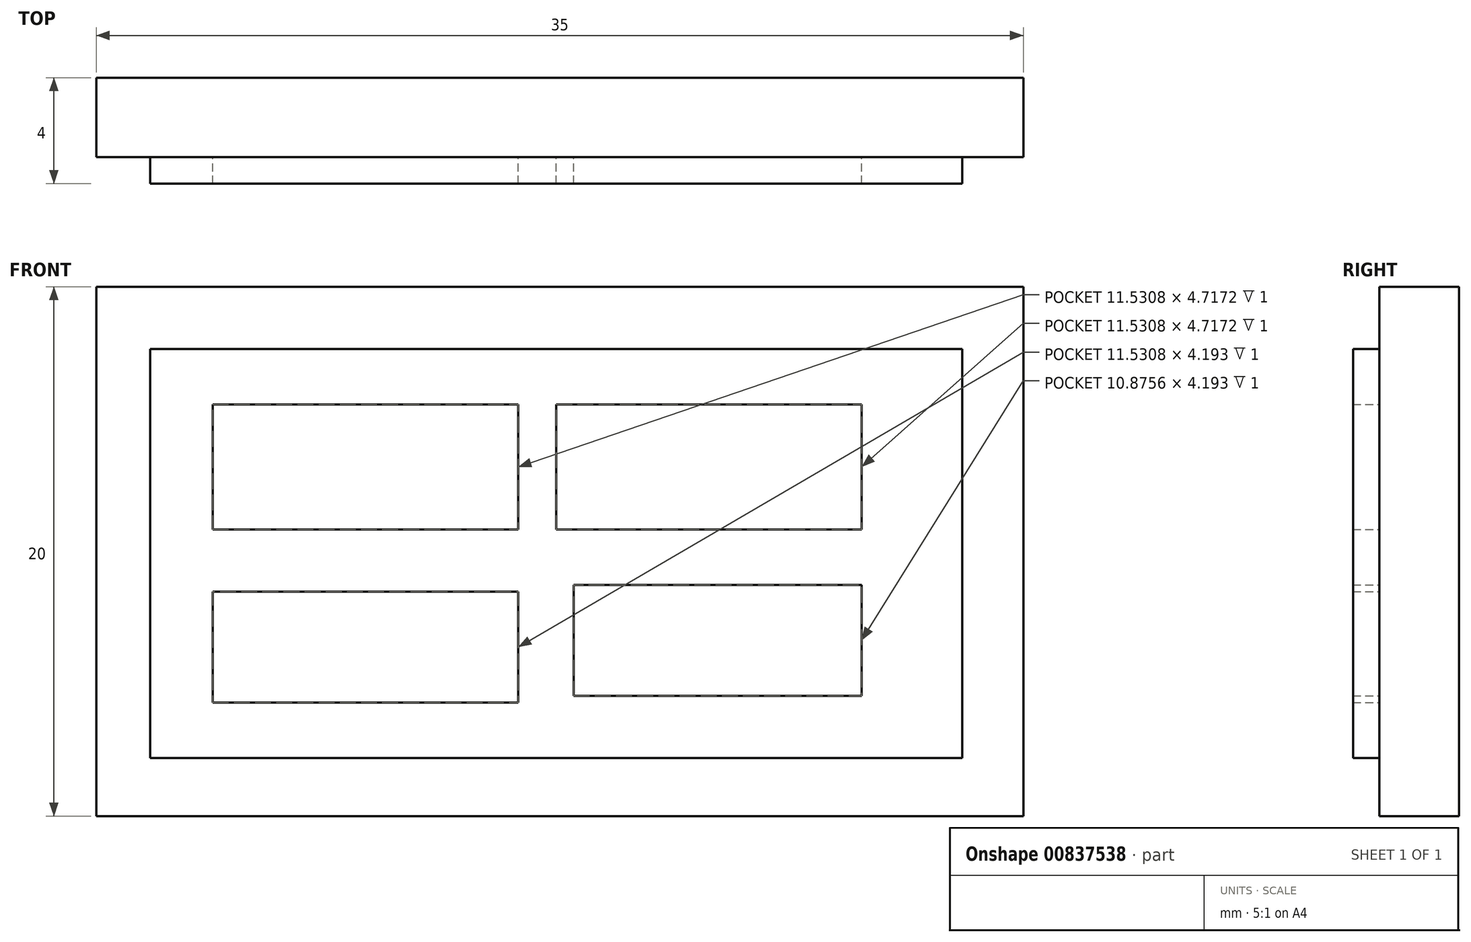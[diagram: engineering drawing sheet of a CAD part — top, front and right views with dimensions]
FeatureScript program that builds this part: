
annotation { "Feature Type Name" : "Feature", "Feature Type Description" : "" }
export const myFeature = defineFeature(function(context is Context, id is Id, definition is map)
    precondition{}
    {
        {
            var Q0;
            Q0=qCreatedBy(makeId("Front.planeOp"),FACE);
            var sketch = newSketch(context, id + "F0", { "sketchPlane" : qUnion([Q0])});
            skLineSegment(sketch, "E0.bottom", {"start": v(-28.9, -6.82) * mm, "end": v(6.1, -6.82) * mm});
            skLineSegment(sketch, "E0.top", {"start": v(-28.9, -26.82) * mm, "end": v(6.1, -26.82) * mm});
            skLineSegment(sketch, "E0.left", {"start": v(-28.9, -6.82) * mm, "end": v(-28.9, -26.82) * mm});
            skLineSegment(sketch, "E0.right", {"start": v(6.1, -6.82) * mm, "end": v(6.1, -26.82) * mm});
            skLineSegment(sketch, "E1.bottom", {"start": v(-26.86, -9.17) * mm, "end": v(3.8, -9.17) * mm});
            skLineSegment(sketch, "E1.top", {"start": v(-26.86, -24.63) * mm, "end": v(3.8, -24.63) * mm});
            skLineSegment(sketch, "E1.left", {"start": v(-26.86, -9.17) * mm, "end": v(-26.86, -24.63) * mm});
            skLineSegment(sketch, "E1.right", {"start": v(3.8, -9.17) * mm, "end": v(3.8, -24.63) * mm});
            skLineSegment(sketch, "E2.bottom", {"start": v(-24.5, -11.27) * mm, "end": v(-12.97, -11.27) * mm});
            skLineSegment(sketch, "E2.top", {"start": v(-24.5, -15.99) * mm, "end": v(-12.97, -15.99) * mm});
            skLineSegment(sketch, "E2.left", {"start": v(-24.5, -11.27) * mm, "end": v(-24.5, -15.99) * mm});
            skLineSegment(sketch, "E2.right", {"start": v(-12.97, -11.27) * mm, "end": v(-12.97, -15.99) * mm});
            skPoint(sketch, "E3.firstSnap0", {"position": v(-11.53, -9.17) * mm});
            skLineSegment(sketch, "E3.bottom", {"start": v(-11.53, -11.27) * mm, "end": v(0, -11.27) * mm});
            skLineSegment(sketch, "E3.top", {"start": v(-11.53, -15.99) * mm, "end": v(0, -15.99) * mm});
            skLineSegment(sketch, "E3.left", {"start": v(-11.53, -11.27) * mm, "end": v(-11.53, -15.99) * mm});
            skLineSegment(sketch, "E3.right", {"start": v(0, -11.27) * mm, "end": v(0, -15.99) * mm});
            skLineSegment(sketch, "E4.bottom", {"start": v(-24.5, -18.34) * mm, "end": v(-12.97, -18.34) * mm});
            skLineSegment(sketch, "E4.top", {"start": v(-24.5, -22.54) * mm, "end": v(-12.97, -22.54) * mm});
            skLineSegment(sketch, "E4.left", {"start": v(-24.5, -18.34) * mm, "end": v(-24.5, -22.54) * mm});
            skLineSegment(sketch, "E4.right", {"start": v(-12.97, -18.34) * mm, "end": v(-12.97, -22.54) * mm});
            skLineSegment(sketch, "E5.bottom", {"start": v(-10.88, -18.08) * mm, "end": v(0, -18.08) * mm});
            skLineSegment(sketch, "E5.top", {"start": v(-10.88, -22.28) * mm, "end": v(0, -22.28) * mm});
            skLineSegment(sketch, "E5.left", {"start": v(-10.88, -18.08) * mm, "end": v(-10.88, -22.28) * mm});
            skLineSegment(sketch, "E5.right", {"start": v(0, -18.08) * mm, "end": v(0, -22.28) * mm});
            skSolve(sketch);
        }
        {
            var Q0;
            Q0=makeQuery(id+"F0.imprint","IMPRINT",FACE,{"disambiguationData":[TD([[makeQuery(id+"F0.imprint","IMPRINT",EDGE,{"derivedFrom":sQuery(id+"F0.wireOp",EDGE,"E1.bottom")}),-1.0]])]});
            extrude(context, id + "F1", {"entities" : qUnion([Q0]), "depth" : 1 * mm, "offsetDistance" : 25 * mm});
        }
        {
            var Q0;
            Q0=makeQuery(id+"F0.imprint","IMPRINT",FACE,{"disambiguationData":[TD([[makeQuery(id+"F0.imprint","IMPRINT",EDGE,{"derivedFrom":sQuery(id+"F0.wireOp",EDGE,"E0.bottom")}),-1.0]])]});
            extrude(context, id + "F2", {"entities" : qUnion([Q0]), "operationType" : NewBodyOperationType.ADD, "depth" : 2 * mm, "offsetDistance" : 25 * mm});
        }
        {
            var Q0;
            Q0 = qSketchRegion(id + "F0", true);
            var Q1;
            Q1=makeQuery(id+"F0.imprint","IMPRINT",FACE,{"disambiguationData":[TD([[makeQuery(id+"F0.imprint","IMPRINT",EDGE,{"derivedFrom":sQuery(id+"F0.wireOp",EDGE,"E3.bottom")}),-1.0]])]});
            var Q2;
            Q2=makeQuery(id+"F0.imprint","IMPRINT",FACE,{"disambiguationData":[TD([[makeQuery(id+"F0.imprint","IMPRINT",EDGE,{"derivedFrom":sQuery(id+"F0.wireOp",EDGE,"E4.bottom")}),-1.0]])]});
            var Q3;
            Q3=makeQuery(id+"F0.imprint","IMPRINT",FACE,{"disambiguationData":[TD([[makeQuery(id+"F0.imprint","IMPRINT",EDGE,{"derivedFrom":sQuery(id+"F0.wireOp",EDGE,"E5.bottom")}),-1.0]])]});
            var Q4;
            Q4=makeQuery(id+"F0.imprint","IMPRINT",FACE,{"disambiguationData":[TD([[makeQuery(id+"F0.imprint","IMPRINT",EDGE,{"derivedFrom":sQuery(id+"F0.wireOp",EDGE,"E2.bottom")}),-1.0]])]});
            var Q5;
            Q5=makeQuery(id+"F1.opExtrude","CAP_FACE",FACE,{"disambiguationData":[OSD([sQuery(id+"F0.wireOp",EDGE,"E1.bottom"),sQuery(id+"F0.wireOp",EDGE,"E1.top"),sQuery(id+"F0.wireOp",EDGE,"E1.left"),sQuery(id+"F0.wireOp",EDGE,"E1.right"),sQuery(id+"F0.wireOp",EDGE,"E2.bottom"),sQuery(id+"F0.wireOp",EDGE,"E2.top"),sQuery(id+"F0.wireOp",EDGE,"E2.left"),sQuery(id+"F0.wireOp",EDGE,"E2.right"),sQuery(id+"F0.wireOp",EDGE,"E3.bottom"),sQuery(id+"F0.wireOp",EDGE,"E3.top"),sQuery(id+"F0.wireOp",EDGE,"E3.left"),sQuery(id+"F0.wireOp",EDGE,"E3.right"),sQuery(id+"F0.wireOp",EDGE,"E4.bottom"),sQuery(id+"F0.wireOp",EDGE,"E4.top"),sQuery(id+"F0.wireOp",EDGE,"E4.left"),sQuery(id+"F0.wireOp",EDGE,"E4.right"),sQuery(id+"F0.wireOp",EDGE,"E5.bottom"),sQuery(id+"F0.wireOp",EDGE,"E5.top"),sQuery(id+"F0.wireOp",EDGE,"E5.left"),sQuery(id+"F0.wireOp",EDGE,"E5.right")])],"isStart":false});
            extrude(context, id + "F3", {"entities" : qUnion([Q0, Q1, Q2, Q3, Q4, Q5]), "operationType" : NewBodyOperationType.ADD, "depth" : 3 * mm, "offsetDistance" : 25 * mm});
        }
    });
